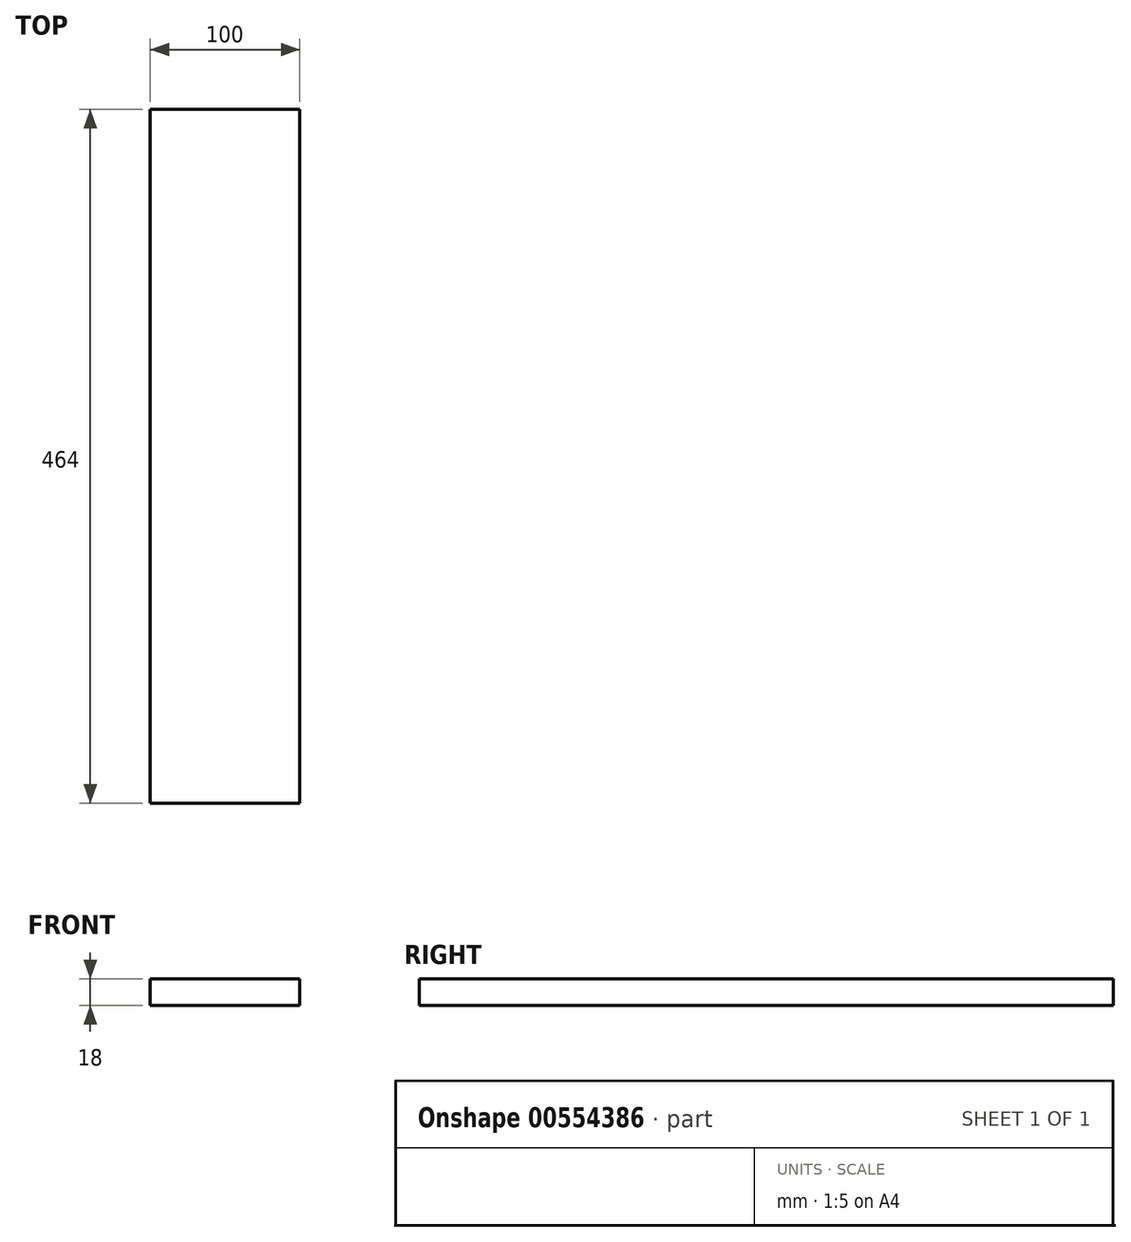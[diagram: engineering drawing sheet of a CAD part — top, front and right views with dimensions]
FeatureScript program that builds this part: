
annotation { "Feature Type Name" : "Feature", "Feature Type Description" : "" }
export const myFeature = defineFeature(function(context is Context, id is Id, definition is map)
    precondition{}
    {
        {
            var Q0;
            Q0=qCreatedBy(makeId("Top.planeOp"),FACE);
            var sketch = newSketch(context, id + "F0", { "sketchPlane" : qUnion([Q0])});
            skLineSegment(sketch, "E0.bottom", {"start": v(0, 0) * mm, "end": v(100, 0) * mm});
            skLineSegment(sketch, "E0.top", {"start": v(0, 464) * mm, "end": v(100, 464) * mm});
            skLineSegment(sketch, "E0.left", {"start": v(0, 0) * mm, "end": v(0, 464) * mm});
            skLineSegment(sketch, "E0.right", {"start": v(100, 0) * mm, "end": v(100, 464) * mm});
            skSolve(sketch);
        }
        {
            var Q0;
            Q0=makeQuery(id+"F0.imprint","IMPRINT",FACE,{"disambiguationData":[TD([[makeQuery(id+"F0.imprint","IMPRINT",EDGE,{"derivedFrom":sQuery(id+"F0.wireOp",EDGE,"E0.bottom")}),1.0]])]});
            extrude(context, id + "F1", {"entities" : qUnion([Q0]), "depth" : 18 * mm, "offsetDistance" : 25 * mm});
        }
    });
